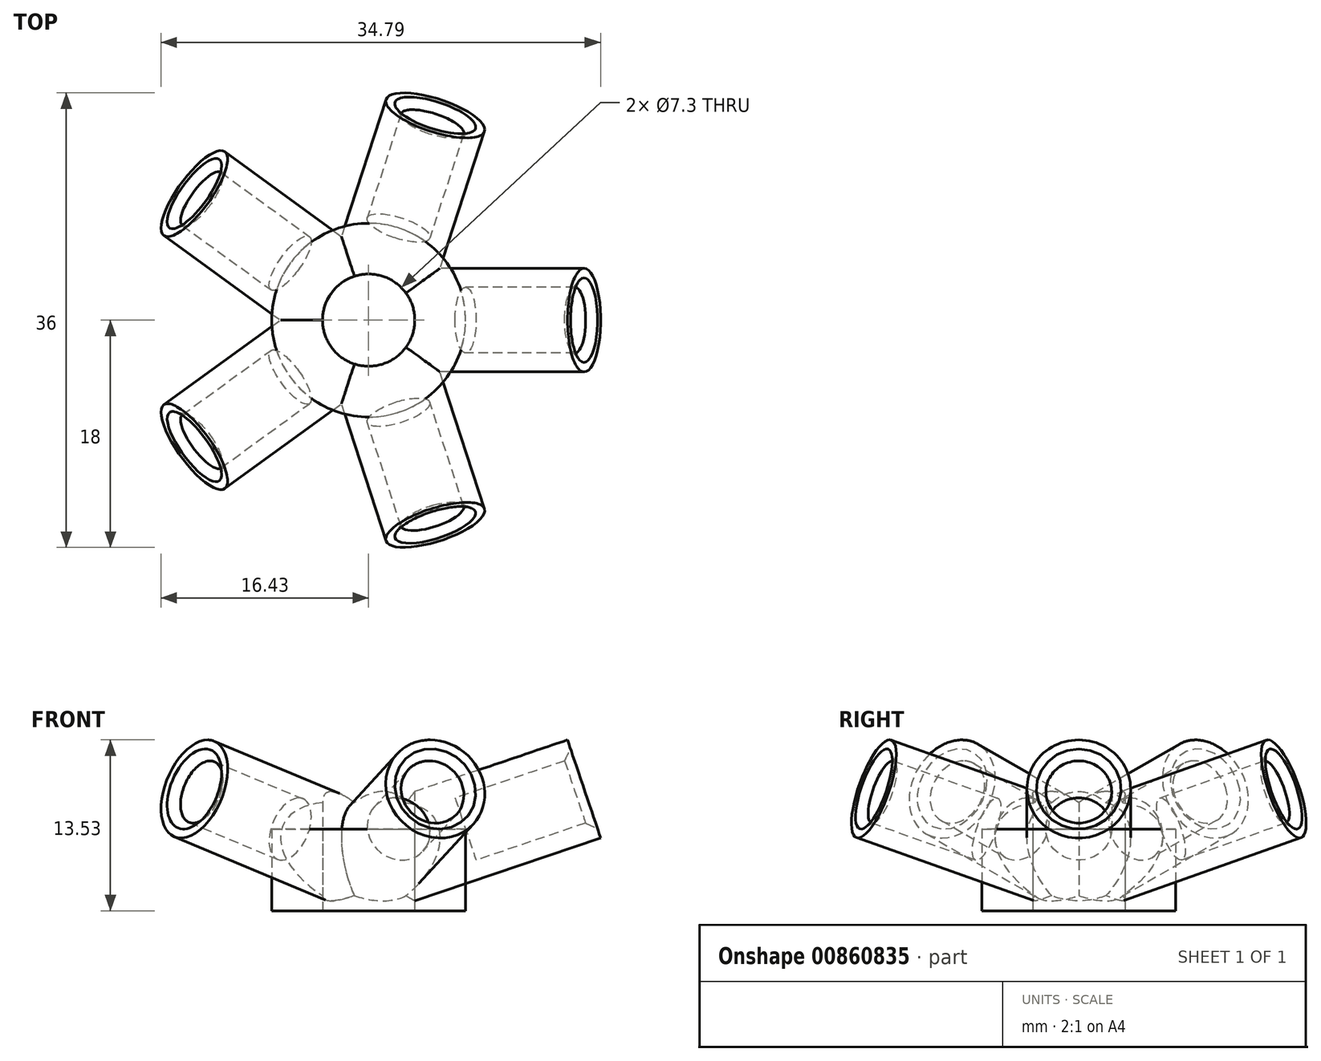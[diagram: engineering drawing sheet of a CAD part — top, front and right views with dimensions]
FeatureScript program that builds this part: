
annotation { "Feature Type Name" : "Feature", "Feature Type Description" : "" }
export const myFeature = defineFeature(function(context is Context, id is Id, definition is map)
    precondition{}
    {
        {
            assignVariable(context, id + "F0", {"name" : "espesor", "anyValue" : 1.5});
        }
        {
            var Q0;
            Q0=qCreatedBy(makeId("Front.planeOp"),FACE);
            var sketch = newSketch(context, id + "F1", { "sketchPlane" : qUnion([Q0])});
            skLineSegment(sketch, "E0", {"start": v(0, 0) * mm, "end": v(17.05, 5.77) * mm, "construction": true});
            skLineSegment(sketch, "E1", {"start": v(0, 0) * mm, "end": v(1.31, -3.88) * mm});
            skLineSegment(sketch, "E2", {"start": v(17.05, 5.77) * mm, "end": v(18.36, 1.88) * mm});
            skLineSegment(sketch, "E3", {"start": v(1.31, -3.88) * mm, "end": v(18.36, 1.88) * mm});
            skLineSegment(sketch, "E4", {"start": v(17.88, 3.3) * mm, "end": v(8.5, 0.13) * mm});
            skLineSegment(sketch, "E5", {"start": v(8.5, 0.13) * mm, "end": v(7.67, 2.6) * mm});
            skLineSegment(sketch, "E6", {"start": v(7.67, 2.6) * mm, "end": v(0, 0) * mm});
            skLineSegment(sketch, "E7", {"start": v(0, 0) * mm, "end": v(0, 41.35) * mm, "construction": true});
            skLineSegment(sketch, "E8", {"start": v(1.31, -3.88) * mm, "end": v(0, -3.88) * mm, "construction": true});
            skLineSegment(sketch, "E9", {"start": v(7.67, 2.6) * mm, "end": v(7.67, -3.88) * mm, "construction": true});
            skLineSegment(sketch, "E10", {"start": v(7.67, -3.88) * mm, "end": v(1.31, -3.88) * mm, "construction": true});
            skLineSegment(sketch, "E11", {"start": v(0, -3.88) * mm, "end": v(7.67, -3.88) * mm});
            skLineSegment(sketch, "E12", {"start": v(7.67, -3.88) * mm, "end": v(7.67, 2.6) * mm});
            skLineSegment(sketch, "E13", {"start": v(0, 2.6) * mm, "end": v(7.67, 2.6) * mm});
            skLineSegment(sketch, "E14", {"start": v(0, 2.6) * mm, "end": v(0, -3.88) * mm});
            skSolve(sketch);
        }
        {
            var Q0;
            {var subQ1=sQuery(id+"F1.wireOp",EDGE,"E4");Q0=makeQuery(id+"F1.imprint","IMPRINT",FACE,{"disambiguationData":[TD([[makeQuery(id+"F1.imprint","IMPRINT",EDGE,{"derivedFrom":subQ1}),1.0]])]});}
            var Q1;
            {var subQ0=sQuery(id+"F1.wireOp",EDGE,"E1");Q1=makeQuery(id+"F1.imprint","IMPRINT",FACE,{"disambiguationData":[TD([[makeQuery(id+"F1.imprint","IMPRINT",EDGE,{"derivedFrom":subQ0}),1.0]])]});}
            var Q2;
            Q2=sQuery(id+"F1.wireOp",EDGE,"E0");
            revolve(context, id + "F2", {"surfaceOperationType" : NewSurfaceOperationType.NEW, "entities" : qUnion([Q0, Q1]), "axis" : qUnion([Q2]), "revolveType" : RevolveType.FULL});
        }
        {
            var Q0;
            Q0=makeQuery(id+"F2.opRevolve","SWEPT_BODY",BODY,{"disambiguationData":[OSD([sQuery(id+"F1.wireOp",EDGE,"E1"),sQuery(id+"F1.wireOp",EDGE,"E2"),sQuery(id+"F1.wireOp",EDGE,"E3"),sQuery(id+"F1.wireOp",EDGE,"E4"),sQuery(id+"F1.wireOp",EDGE,"E5"),sQuery(id+"F1.wireOp",EDGE,"E6")])]});
            var Q1;
            Q1=sQuery(id+"F1.wireOp",EDGE,"E7");
            circularPattern(context, id + "F3", {"operationType" : NewBodyOperationType.ADD, "entities" : qUnion([Q0]), "axis" : qUnion([Q1]), "angle" : 360 * degree, "instanceCount" : 5, "equalSpace" : true});
        }
        {
            var Q0;
            {var subQ0=sQuery(id+"F1.wireOp",EDGE,"E1");Q0=makeQuery(id+"F1.imprint","IMPRINT",FACE,{"disambiguationData":[TD([[makeQuery(id+"F1.imprint","IMPRINT",EDGE,{"derivedFrom":subQ0}),-1.0]])]});}
            var Q1;
            {var subQ0=sQuery(id+"F1.wireOp",EDGE,"E1");Q1=makeQuery(id+"F1.imprint","IMPRINT",FACE,{"disambiguationData":[TD([[makeQuery(id+"F1.imprint","IMPRINT",EDGE,{"derivedFrom":subQ0}),1.0]])]});}
            var Q2;
            {var subQ0=sQuery(id+"F1.wireOp",EDGE,"E11");var subQ3=sQuery(id+"F1.wireOp",EDGE,"E12");var subQ5=makeQuery(id+"F1.imprint","INTERSECT",VERTEX,{"derivedFrom":[subQ0,subQ3]});Q2=makeQuery(id+"F1.imprint","IMPRINT",FACE,{"disambiguationData":[TD([[makeQuery(id+"F1.imprint","IMPRINT",EDGE,{"disambiguationData":[TD([[subQ5,-1.0]])],"derivedFrom":subQ3}),1.0]])]});}
            var Q3;
            {var subQ0=sQuery(id+"F1.wireOp",EDGE,"E6");Q3=makeQuery(id+"F1.imprint","IMPRINT",FACE,{"disambiguationData":[TD([[makeQuery(id+"F1.imprint","IMPRINT",EDGE,{"derivedFrom":subQ0}),-1.0]])]});}
            var Q4;
            Q4=sQuery(id+"F1.wireOp",EDGE,"E13");
            var Q5;
            Q5=sQuery(id+"F1.wireOp",EDGE,"E14");
            var Q6;
            Q6=sQuery(id+"F1.wireOp",EDGE,"E7");
            revolve(context, id + "F4", {"surfaceOperationType" : NewSurfaceOperationType.NEW, "entities" : qUnion([Q0, Q1, Q2, Q3]), "surfaceEntities" : qUnion([Q4, Q5]), "axis" : qUnion([Q6]), "revolveType" : RevolveType.FULL});
        }
        {
            var Q0;
            Q0=makeQuery(id+"F4.opRevolve","SWEPT_FACE",FACE,{"disambiguationData":[OSD([sQuery(id+"F1.wireOp",EDGE,"E11")])]});
            var sketch = newSketch(context, id + "F5", { "sketchPlane" : qUnion([Q0])});
            skCircle(sketch, "E15", {"center": v(0, 0) * mm, "radius": 3.65 * mm});
            skSolve(sketch);
        }
        {
            var Q0;
            Q0=makeQuery(id+"F5.imprint","IMPRINT",FACE,{"disambiguationData":[TD([[makeQuery(id+"F5.imprint","IMPRINT",EDGE,{"derivedFrom":sQuery(id+"F5.wireOp",EDGE,"E15")}),1.0]])]});
            extrude(context, id + "F6", {"entities" : qUnion([Q0]), "operationType" : NewBodyOperationType.REMOVE, "endBound" : BoundingType.THROUGH_ALL, "oppositeDirection" : true, "depth" : 25 * mm, "offsetDistance" : 25 * mm});
        }
        {
            var Q0;
            Q0=makeQuery(id+"F3.opPattern","COPY",EDGE,{"derivedFrom":makeQuery(id+"F2.opRevolve","SWEPT_EDGE",EDGE,{"disambiguationData":[OSD([sQuery(id+"F1.wireOp",EDGE,"E2"),sQuery(id+"F1.wireOp",EDGE,"E4")])]}),"instanceName":"3"});
            var Q1;
            Q1=makeQuery(id+"F3.opPattern","COPY",EDGE,{"derivedFrom":makeQuery(id+"F2.opRevolve","SWEPT_EDGE",EDGE,{"disambiguationData":[OSD([sQuery(id+"F1.wireOp",EDGE,"E2"),sQuery(id+"F1.wireOp",EDGE,"E4")])]}),"instanceName":"4"});
            var Q2;
            Q2=makeQuery(id+"F2.opRevolve","SWEPT_EDGE",EDGE,{"disambiguationData":[OSD([sQuery(id+"F1.wireOp",EDGE,"E2"),sQuery(id+"F1.wireOp",EDGE,"E4")])]});
            var Q3;
            Q3=makeQuery(id+"F3.opPattern","COPY",EDGE,{"derivedFrom":makeQuery(id+"F2.opRevolve","SWEPT_EDGE",EDGE,{"disambiguationData":[OSD([sQuery(id+"F1.wireOp",EDGE,"E2"),sQuery(id+"F1.wireOp",EDGE,"E4")])]}),"instanceName":"1"});
            var Q4;
            Q4=makeQuery(id+"F3.opPattern","COPY",EDGE,{"derivedFrom":makeQuery(id+"F2.opRevolve","SWEPT_EDGE",EDGE,{"disambiguationData":[OSD([sQuery(id+"F1.wireOp",EDGE,"E2"),sQuery(id+"F1.wireOp",EDGE,"E4")])]}),"instanceName":"2"});
            chamfer(context, id + "F7", {"entities" : qUnion([Q0, Q1, Q2, Q3, Q4]), "width" : (getVariable(context, 'espesor') / 2) * mm, "tangentPropagation" : true});
        }
    });
